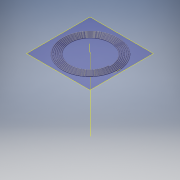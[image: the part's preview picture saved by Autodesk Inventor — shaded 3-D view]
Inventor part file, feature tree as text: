
AUTODESK INVENTOR PART (.ipt)
format: ipt  version: 2019 (Build 230136000, 136)  size: 459,264 bytes
history: native  units: mm
features: other x10, reference x4, sketch x1, helix x1
ambient origin geometry x8: Origin, YZ Plane, XZ Plane, XY Plane, X Axis, Y Axis, Z Axis, Center Point
bodies: Body1 (feature_tree)
feature tree (16):
  other  "Твердое тело1"
  sketch  "Эскиз1"
  other  "РабОсь1"
  other  "РабПлоскость2"
  other  "РабОсь2"
  other  "Пружина1"
  reference  "Ссылка1"
  other  "РабПлоскость1"
  reference  "Ссылка3"
  reference  "Ссылка4"
  reference  "Ссылка5"
  other  "<userpath>\Documents\GitHub\Tesla_coil_V1\3dModels\TeslaCoil.iam"
  other  "TeslaCoil.iam"
  other  "PrimaryTab:1"
  other  "RackeSecondary:4"
  helix  "Coil:1"  [1 undecoded]
note: 1 required parameter value undecoded (feature->parameter linkage not recoverable at this tier; creation-order binding heuristic only, values carry confidence <= 0.55)
